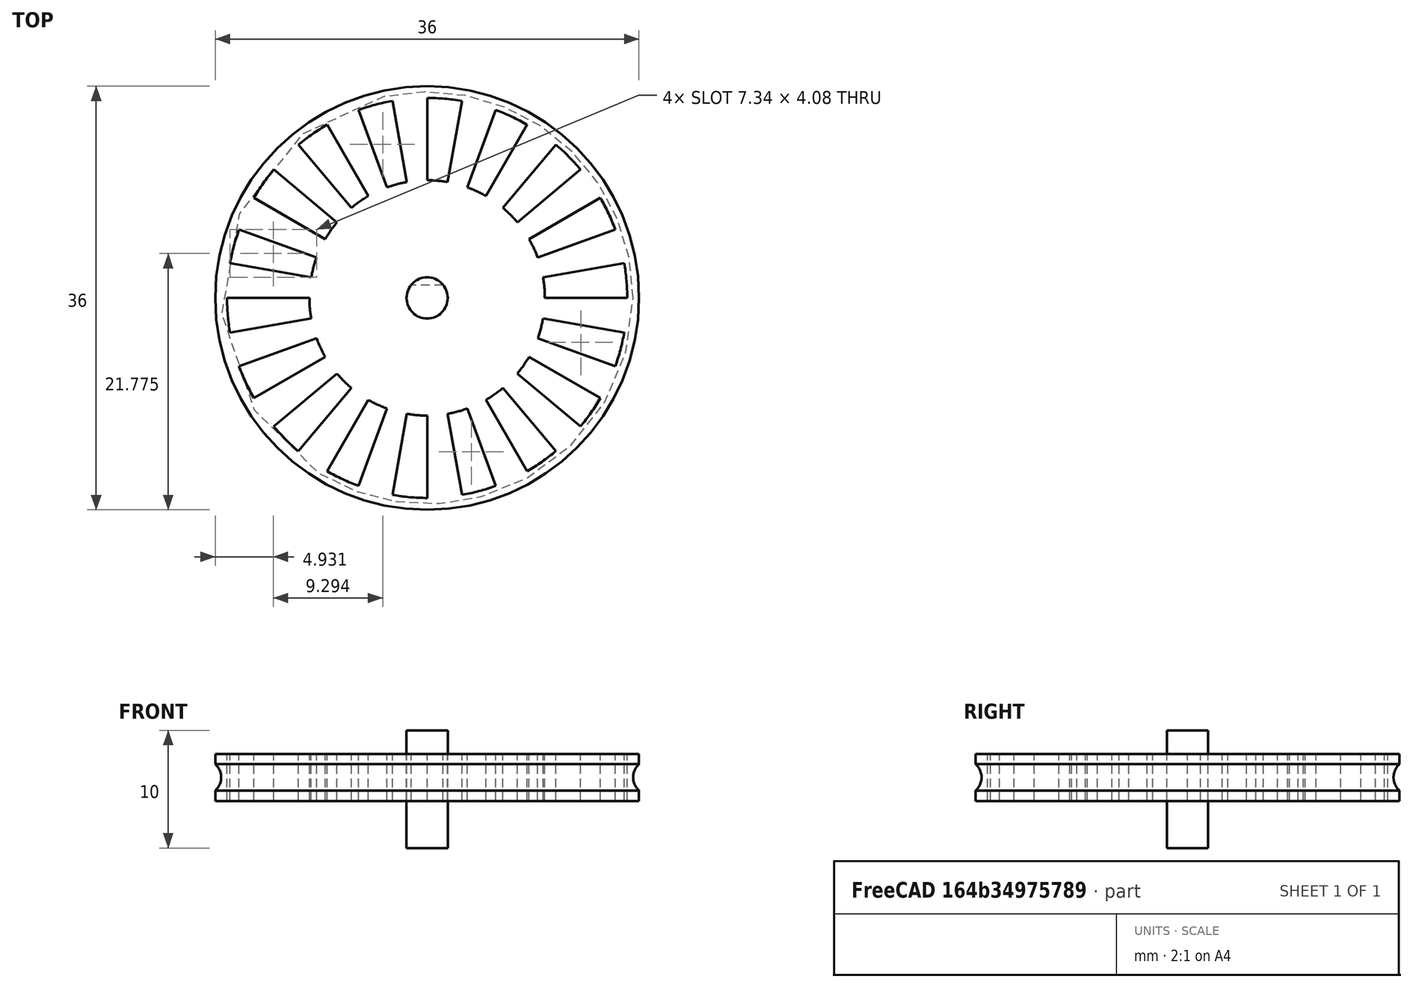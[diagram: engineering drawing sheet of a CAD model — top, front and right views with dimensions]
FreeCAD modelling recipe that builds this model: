
FCSTD DOCUMENT  (FreeCAD 0.17R13522 (Git))
Label: wheel 1.75 hole
License: All rights reserved
LicenseURL: http://en.wikipedia.org/wiki/All_rights_reserved
objects: Part::Feature×17, Part::Cut×8, Part::Cylinder×5, Part::Box×3, Part::Torus×2, Part::MultiFuse×1
note: 36 computed .brp shape members not serialized (recipe doc carries the construction recipe); baked Part::Feature solids carry a one-line shape summary decoded from their .brp

FEATURE [Part::Cylinder] Cylinder012  label="wheel1a"
  Angle = 360
  AttacherType = Attacher::AttachEngine3D
  Height = 4
  Radius = 18
FEATURE [Part::Cylinder] Cylinder028  label="Cylinder024"
  Angle = 360
  AttacherType = Attacher::AttachEngine3D
  Height = 10
  Placement = pos=(0,0,-1) rot=(0,0,1;0rad)
  Radius = 1.75
FEATURE [Part::Box] Box084016  label="Cube067"
  AttacherType = Attacher::AttachEngine3D
  Height = 12
  Length = 10
  Placement = pos=(-5,1.1,-1.5) rot=(0,0,1;0rad)
  Width = 10
FEATURE [Part::Cut] Cut057
  Base = -> Cylinder028
  Tool = -> Box084016
FEATURE [Part::Cut] Cut062
  Base = -> Cylinder012
  Tool = -> Cut057
FEATURE [Part::Torus] Torus002
  Angle1 = -180
  Angle2 = 180
  Angle3 = 360
  AttacherType = Attacher::AttachEngine3D
  Placement = pos=(0,0,2) rot=(0,0,1;0rad)
  Radius1 = 19
  Radius2 = 1.5
FEATURE [Part::Cut] Cut063  label="wheel"
  Base = -> Cut062
  Placement = pos=(0,-20,48) rot=(0,0,1;0rad)
  Tool = -> Torus002
FEATURE [Part::Torus] Torus
  Angle1 = -180
  Angle2 = 180
  Angle3 = 360
  AttacherType = Attacher::AttachEngine3D
  Placement = pos=(0,-20,50) rot=(0,0,1;0rad)
  Radius1 = 19
  Radius2 = 1.5
FEATURE [Part::Cylinder] Cylinder062  label="Cylinder158"
  Angle = 360
  AttacherType = Attacher::AttachEngine3D
  Height = 10
  Radius = 17
FEATURE [Part::Cylinder] Cylinder063  label="Cylinder159"
  Angle = 360
  AttacherType = Attacher::AttachEngine3D
  Height = 16
  Placement = pos=(0,0,-4) rot=(0,0,1;0rad)
  Radius = 10
FEATURE [Part::Cut] Cut044
  Base = -> Cylinder062
  Tool = -> Cylinder063
FEATURE [Part::Box] Box026  label="Cube025"
  AttacherType = Attacher::AttachEngine3D
  Height = 20
  Length = 18
  Placement = pos=(0,0,-5) rot=(0,0,1;0rad)
  Width = 20
FEATURE [Part::Box] Box027  label="Cube026"
  AttacherType = Attacher::AttachEngine3D
  Height = 20
  Length = 10
  Placement = pos=(0,0,-5) rot=(0,0,1;0.174533rad)
  Width = 20
FEATURE [Part::Cut] Cut045
  Base = -> Box027
  Tool = -> Box026
FEATURE [Part::Feature] Cut045001
  Placement = pos=(0,0,0) rot=(0,0,1;0.349066rad)
  shape: bbox 10 x 22.32 x 20 mm, 7 faces (baked)
FEATURE [Part::Feature] Cut045002
  Placement = pos=(0,0,0) rot=(0,0,1;0.698132rad)
  shape: bbox 15.32 x 20.52 x 20 mm, 7 faces (baked)
FEATURE [Part::Feature] Cut045003
  Placement = pos=(0,0,0) rot=(0,0,1;1.0472rad)
  shape: bbox 18.79 x 16.24 x 20 mm, 7 faces (baked)
FEATURE [Part::Feature] Cut045004
  Placement = pos=(0,0,0) rot=(0,0,1;1.39626rad)
  shape: bbox 20 x 10 x 20 mm, 7 faces (baked)
FEATURE [Part::Feature] Cut045005
  Placement = pos=(0,0,0) rot=(0,0,1;1.74533rad)
  shape: bbox 22.21 x 9.894 x 20 mm, 7 faces (baked)
FEATURE [Part::Feature] Cut045006
  Placement = pos=(0,0,0) rot=(0,0,1;2.0944rad)
  shape: bbox 21.75 x 12.86 x 20 mm, 7 faces (baked)
FEATURE [Part::Feature] Cut045007
  Placement = pos=(0,0,0) rot=(0,0,1;2.44346rad)
  shape: bbox 18.66 x 17.32 x 20 mm, 7 faces (baked)
FEATURE [Part::Feature] Cut045008
  Placement = pos=(0,0,0) rot=(0,0,1;2.79253rad)
  shape: bbox 13.32 x 19.7 x 20 mm, 7 faces (baked)
FEATURE [Part::Feature] Cut045009
  Placement = pos=(0,0,0) rot=(0,0,1;3.14159rad)
  shape: bbox 10.1 x 21.43 x 20 mm, 7 faces (baked)
FEATURE [Part::Feature] Cut045010
  Placement = pos=(0,0,0) rot=(0,0,1;3.49066rad)
  shape: bbox 10 x 22.32 x 20 mm, 7 faces (baked)
FEATURE [Part::Feature] Cut045011
  Placement = pos=(0,0,0) rot=(0,0,1;3.83972rad)
  shape: bbox 15.32 x 20.52 x 20 mm, 7 faces (baked)
FEATURE [Part::Feature] Cut045012
  Placement = pos=(0,0,0) rot=(0,0,1;4.18879rad)
  shape: bbox 18.79 x 16.24 x 20 mm, 7 faces (baked)
FEATURE [Part::Feature] Cut045013
  Placement = pos=(0,0,0) rot=(0,0,-1;1.74533rad)
  shape: bbox 20 x 10 x 20 mm, 7 faces (baked)
FEATURE [Part::Feature] Cut045014
  Placement = pos=(0,0,0) rot=(0,0,-1;1.39626rad)
  shape: bbox 22.21 x 9.894 x 20 mm, 7 faces (baked)
FEATURE [Part::Feature] Cut045015
  Placement = pos=(0,0,0) rot=(0,0,-1;1.0472rad)
  shape: bbox 21.75 x 12.86 x 20 mm, 7 faces (baked)
FEATURE [Part::Feature] Cut045016
  Placement = pos=(0,0,0) rot=(0,0,-1;0.698132rad)
  shape: bbox 18.66 x 17.32 x 20 mm, 7 faces (baked)
FEATURE [Part::Feature] Cut045017
  Placement = pos=(0,0,0) rot=(0,0,-1;0.349066rad)
  shape: bbox 13.32 x 19.7 x 20 mm, 7 faces (baked)
FEATURE [Part::MultiFuse] Fusion095
  Shapes = -> [Cut045001,Cut045008,Cut045010,Cut045009,Cut045005,Cut045003,Cut045006,Cut045002,Cut045004,Cut045007,Cut045016,Cut045017,Cut045011,Cut045012,Cut045013,Cut045014,Cut045015,Cut045]
FEATURE [Part::Cut] Cut045018
  Base = -> Cut044
  Placement = pos=(0,-20,43) rot=(0,1,0;0rad)
  Tool = -> Fusion095
FEATURE [Part::Cylinder] Cylinder064  label="Cylinder160"
  Angle = 360
  AttacherType = Attacher::AttachEngine3D
  Height = 10
  Placement = pos=(0,-20,44) rot=(0,0,1;0rad)
  Radius = 1.75
FEATURE [Part::Cut] Cut
  Base = -> Cut063
  Tool = -> Cut045018
FEATURE [Part::Cut] Cut045019
  Base = -> Cut
  Tool = -> Torus
